FCSTD DOCUMENT  (FreeCAD 0.19R0.19.2)
Label: laptopStand005
License: All rights reserved
LicenseURL: http://en.wikipedia.org/wiki/All_rights_reserved
objects: Sketcher::SketchObject×1
note: 1 computed .brp shape members not serialized (recipe doc carries the construction recipe); baked Part::Feature solids carry a one-line shape summary decoded from their .brp

FEATURE [Sketcher::SketchObject] Sketch
  FullyConstrained = false
  sketch-geometry (52):
    g0: LineSegment StartX=-22.9272 StartY=136.221 StartZ=0 EndX=-22.9272 EndY=-103.779 EndZ=0
    g1: LineSegment StartX=-22.9272 StartY=136.221 StartZ=0 EndX=387.073 EndY=136.221 EndZ=0
    g2: LineSegment StartX=66.1121 StartY=95.2117 StartZ=0 EndX=66.1121 EndY=-84.7883 EndZ=0
    g3: LineSegment StartX=66.1121 StartY=95.2117 StartZ=0 EndX=256.112 EndY=95.2117 EndZ=0
    g4: LineSegment StartX=256.112 StartY=83.2117 StartZ=0 EndX=78.1121 EndY=83.2117 EndZ=0
    g5: LineSegment StartX=78.1121 StartY=-84.7883 StartZ=0 EndX=78.1121 EndY=83.2117 EndZ=0
    g6: LineSegment StartX=286.112 StartY=95.2117 StartZ=0 EndX=286.112 EndY=89.2117 EndZ=0
    g7-g11: Circle x5 (B-spline internal-alignment scaffolding for g12; pole/knot coordinates omitted)
    g12: BSplineCurve PolesCount=5 KnotsCount=3 Degree=3 IsPeriodic=0
    g13: GeomPoint X=271.112 Y=85.2117 Z=0
    g14: GeomPoint X=258.112 Y=89.2117 Z=0
    g15: GeomPoint X=271.112 Y=89.2117 Z=0
    g16-g20: Circle x5 (B-spline internal-alignment scaffolding for g21; pole/knot coordinates omitted)
    g21: BSplineCurve PolesCount=5 KnotsCount=3 Degree=3 IsPeriodic=0
    g22: GeomPoint X=271.112 Y=93.2117 Z=0
    g23: GeomPoint X=284.112 Y=89.2117 Z=0
    g24: GeomPoint X=271.112 Y=89.2117 Z=0
    g25: LineSegment StartX=256.112 StartY=95.2117 StartZ=0 EndX=271.112 EndY=95.2117 EndZ=0
    g26: LineSegment StartX=271.112 StartY=93.2117 StartZ=0 EndX=271.112 EndY=95.2117 EndZ=0
    g27: LineSegment StartX=271.112 StartY=85.2117 StartZ=0 EndX=271.112 EndY=83.2117 EndZ=0
    g28: LineSegment StartX=271.112 StartY=83.2117 StartZ=0 EndX=256.112 EndY=83.2117 EndZ=0
    g29: LineSegment StartX=329.695 StartY=81.7679 StartZ=0 EndX=507.695 EndY=81.7679 EndZ=0
    g30: LineSegment StartX=329.695 StartY=93.7679 StartZ=0 EndX=519.695 EndY=93.7679 EndZ=0
    g31-g34: Circle x4 (B-spline internal-alignment scaffolding for g35; pole/knot coordinates omitted)
    g35: BSplineCurve PolesCount=5 KnotsCount=3 Degree=3 IsPeriodic=0
    g36: GeomPoint X=314.695 Y=83.7679 Z=0
    g37: GeomPoint X=301.695 Y=87.7679 Z=0
    g38: GeomPoint X=314.695 Y=87.7679 Z=0
    g39-g43: Circle x5 (B-spline internal-alignment scaffolding for g44; pole/knot coordinates omitted)
    g44: BSplineCurve PolesCount=5 KnotsCount=3 Degree=3 IsPeriodic=0
    g45: GeomPoint X=314.695 Y=91.7679 Z=0
    g46: GeomPoint X=327.695 Y=87.7679 Z=0
    g47: GeomPoint X=314.695 Y=87.7679 Z=0
    g48: LineSegment StartX=314.695 StartY=91.7679 StartZ=0 EndX=314.695 EndY=93.7679 EndZ=0
    g49: LineSegment StartX=329.695 StartY=81.7679 StartZ=0 EndX=314.695 EndY=81.7679 EndZ=0
    g50: LineSegment StartX=314.695 StartY=83.7679 StartZ=0 EndX=314.695 EndY=81.7679 EndZ=0
    g51: LineSegment StartX=329.695 StartY=93.7679 StartZ=0 EndX=314.695 EndY=93.7679 EndZ=0
  constraints (75):
    c: Vertical(g0)
    c: Distance(g0) = 240
    c: Horizontal(g1)
    c: Distance(g1) = 410
    c: Coincident(g1,g0)
    c: Vertical(g2)
    c: Distance(g2) = 180
    c: Horizontal(g3)
    c: Distance(g3) = 190
    c: Coincident(g3,g2)
    c: Block(g2)
    c: Horizontal(g4)
    c: Vertical(g5)
    c: Coincident(g4,g5)
    c: Block(g4)
    c: Block(g5)
    c: Vertical(g6)
    c: Distance(g6) = 6
    c: Weight(g7) = 1
    c: Equal(g7, g8-g11) x4
    c: InternalAlignment(g7-g11 -> g12) x5
    c: InternalAlignment(g13,g12)
    c: InternalAlignment(g14,g12)
    c: InternalAlignment(g15,g12)
    c: Weight(g16) = 1
    c: Equal(g16,g17)
    c: Equal(g16,g18)
    c: Coincident(g18,g6)
    c: Equal(g16,g19)
    c: Equal(g16,g20)
    c: InternalAlignment(g16-g20 -> g21) x5
    c: InternalAlignment(g22,g21)
    c: InternalAlignment(g23,g21)
    c: InternalAlignment(g24,g21)
    c: Block(g21)
    c: Block(g12)
    c: Coincident(g25,g3)
    c: Horizontal(g25)
    c: Coincident(g26,g21)
    c: Vertical(g26)
    c: Coincident(g25,g26)
    c: Coincident(g27,g12)
    c: Vertical(g27)
    c: Coincident(g28,g4)
    c: Horizontal(g28)
    c: Block(g27)
    c: Block(g28)
    c: Horizontal(g29)
    c: Horizontal(g30)
    c: Block(g30)
    c: Equal(g31,g32)
    c: Equal(g31,g33)
    c: Equal(g31,g34)
    c: InternalAlignment(g31-g34 -> g35) x4
    c: InternalAlignment(g36,g35)
    c: InternalAlignment(g37,g35)
    c: InternalAlignment(g38,g35)
    c: Equal(g39, g40-g43) x4
    c: InternalAlignment(g39-g43 -> g44) x5
    c: InternalAlignment(g45,g44)
    c: InternalAlignment(g46,g44)
    c: InternalAlignment(g47,g44)
    c: Block(g44)
    c: Block(g35)
    c: Coincident(g48,g44)
    c: Vertical(g48)
    c: Block(g29)
    c: Coincident(g49,g29)
    c: Horizontal(g49)
    c: Coincident(g50,g35)
    c: Vertical(g50)
    c: Coincident(g50,g49)
    c: Coincident(g51,g30)
    c: Coincident(g51,g48)
    c: Horizontal(g51)
